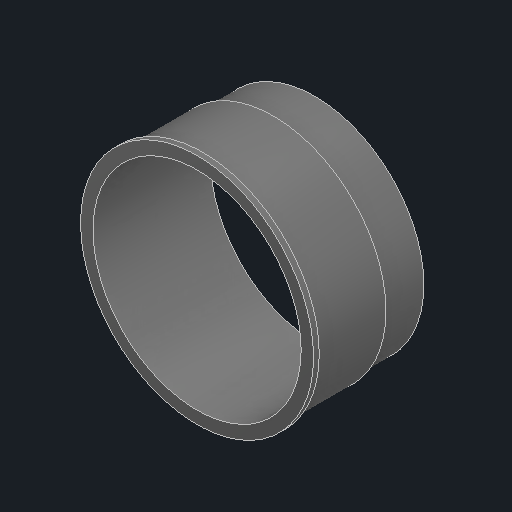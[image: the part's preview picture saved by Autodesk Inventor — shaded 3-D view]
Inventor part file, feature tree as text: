
AUTODESK INVENTOR PART (.ipt)
format: ipt  version: 2025 (Build 290162000, 162)  size: 117,248 bytes
history: native  units: in
note: dims shown in document units (in); Inventor stores cm internally (conversion verified against a paired STEP export)
features: revolve x1
ambient origin geometry x8: Origin, YZ Plane, XZ Plane, XY Plane, X Axis, Y Axis, Z Axis, Center Point
bodies: Solid1 (feature_tree)
feature tree (1):
  revolve  "Revolve2"  [1 undecoded]
note: 1 required parameter value undecoded (feature->parameter linkage not recoverable at this tier; creation-order binding heuristic only, values carry confidence <= 0.55)
